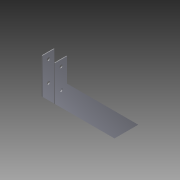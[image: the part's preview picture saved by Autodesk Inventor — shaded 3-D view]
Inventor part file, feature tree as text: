
AUTODESK INVENTOR PART (.ipt)
format: ipt  version: 2012 (Build 160160000, 160)  size: 101,888 bytes
history: native  units: in
note: dims shown in document units (in); Inventor stores cm internally (conversion verified against a paired STEP export)
features: extrude x2, sketch x2
ambient origin geometry x8: Origin, YZ Plane, XZ Plane, XY Plane, X Axis, Y Axis, Z Axis, Center Point
bodies: Solid1 (feature_tree)
feature tree (4):
  extrude  "Extrusion1"  Depth=8.0in
  extrude  "Extrusion2"  Depth=0.0625in
  sketch  "Sketch1"  dims[d0=1.125in d1=8.0in]
  sketch  "Sketch2"  dims[d2=0.0625in d3=0.0625in d4=0.0625in d5=7.0in d6=0.0in d7=2.0in d8=45.0deg d9=1.0in d10=0.25in d11=0.5in d12=0.5in d13=1.732in d14=8.0in d15=0.0in]
